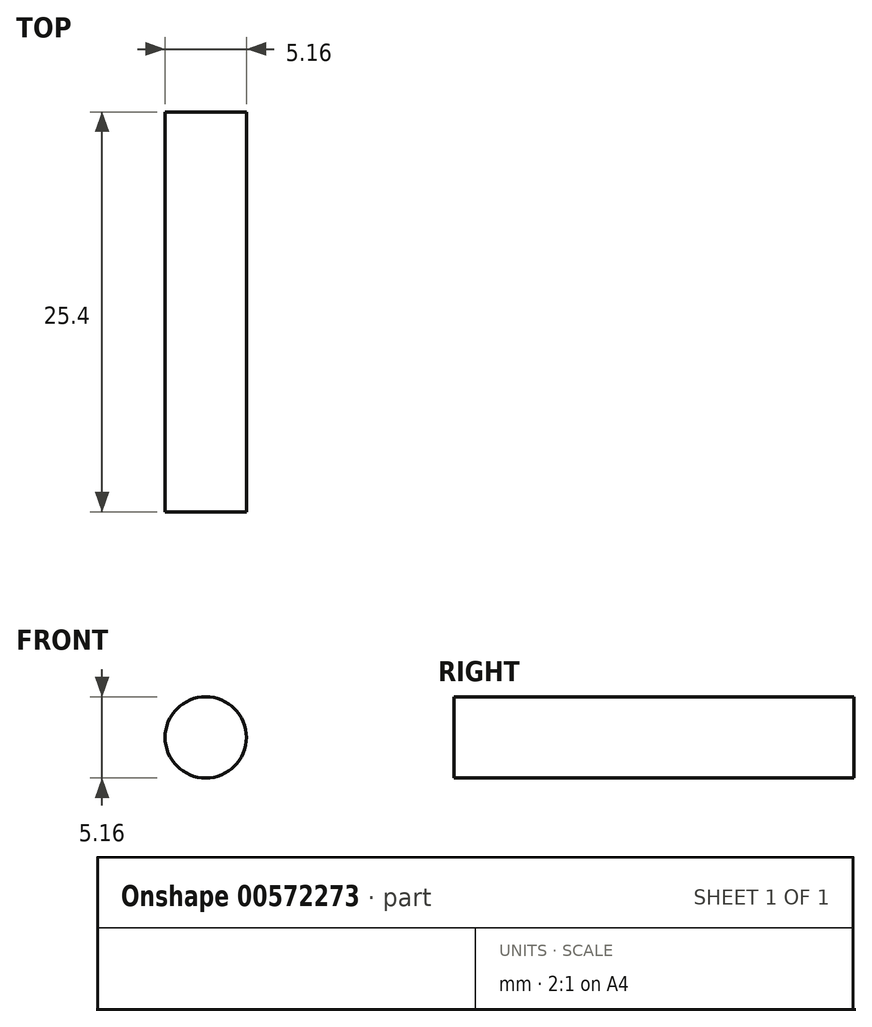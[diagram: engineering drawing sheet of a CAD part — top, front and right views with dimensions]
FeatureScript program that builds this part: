
annotation { "Feature Type Name" : "Feature", "Feature Type Description" : "" }
export const myFeature = defineFeature(function(context is Context, id is Id, definition is map)
    precondition{}
    {
        {
            var Q0;
            Q0=qCreatedBy(makeId("Front.planeOp"),FACE);
            var sketch = newSketch(context, id + "F0", { "sketchPlane" : qUnion([Q0])});
            skCircle(sketch, "E0", {"center": v(0, 0) * mm, "radius": 2.58 * mm});
            skSolve(sketch);
        }
        {
            var Q0;
            Q0 = qSketchRegion(id + "F0", true);
            extrude(context, id + "F1", {"entities" : qUnion([Q0]), "depth" : 25.4 * mm, "offsetDistance" : 25.4 * mm});
        }
    });
